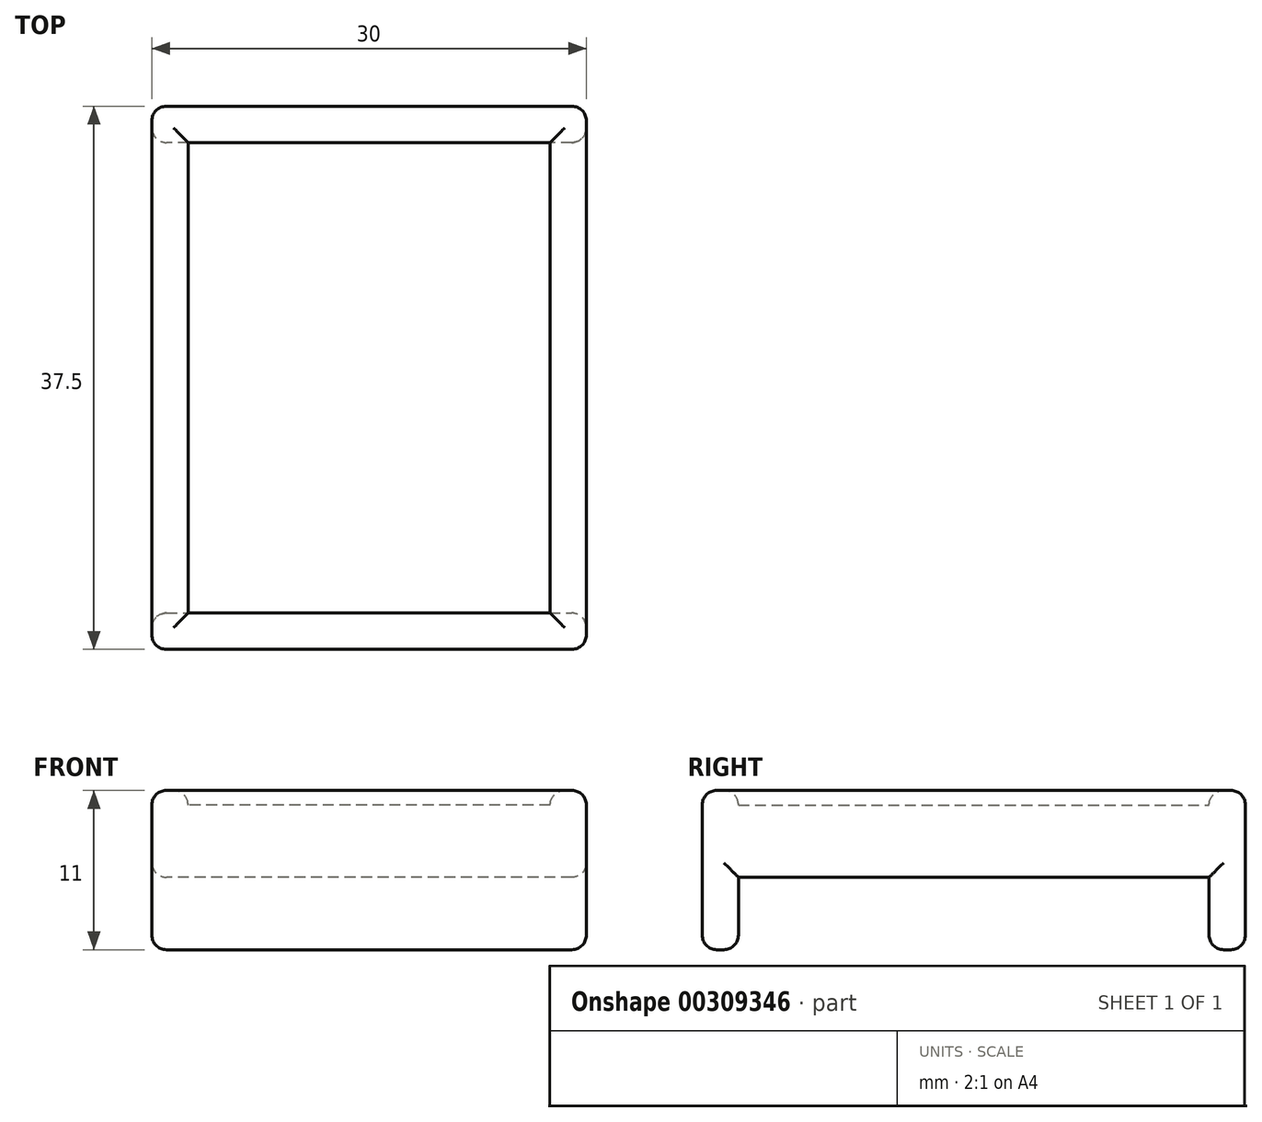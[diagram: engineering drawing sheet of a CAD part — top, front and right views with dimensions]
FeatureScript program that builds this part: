
annotation { "Feature Type Name" : "Feature", "Feature Type Description" : "" }
export const myFeature = defineFeature(function(context is Context, id is Id, definition is map)
    precondition{}
    {
        {
            var Q0;
            Q0=qCreatedBy(makeId("Top.planeOp"),FACE);
            var sketch = newSketch(context, id + "F0", { "sketchPlane" : qUnion([Q0])});
            skLineSegment(sketch, "E0.bottom", {"start": v(-12.5, 16.25) * mm, "end": v(12.5, 16.25) * mm});
            skLineSegment(sketch, "E0.top", {"start": v(-12.5, -16.25) * mm, "end": v(12.5, -16.25) * mm});
            skLineSegment(sketch, "E0.left", {"start": v(-12.5, 16.25) * mm, "end": v(-12.5, -16.25) * mm});
            skLineSegment(sketch, "E0.right", {"start": v(12.5, 16.25) * mm, "end": v(12.5, -16.25) * mm});
            skPoint(sketch, "E0.middle", {"position": v(0, 0) * mm});
            skLineSegment(sketch, "E1.bottom", {"start": v(-15, 18.75) * mm, "end": v(15, 18.75) * mm});
            skLineSegment(sketch, "E1.top", {"start": v(-15, -18.75) * mm, "end": v(15, -18.75) * mm});
            skLineSegment(sketch, "E1.left", {"start": v(-15, 18.75) * mm, "end": v(-15, -18.75) * mm});
            skLineSegment(sketch, "E1.right", {"start": v(15, 18.75) * mm, "end": v(15, -18.75) * mm});
            skLineSegment(sketch, "E2", {"start": v(-12.5, 16.25) * mm, "end": v(-15, 16.25) * mm});
            skLineSegment(sketch, "E3", {"start": v(12.5, 16.25) * mm, "end": v(15, 16.25) * mm});
            skLineSegment(sketch, "E4", {"start": v(-12.5, -16.25) * mm, "end": v(-15, -16.25) * mm});
            skLineSegment(sketch, "E5", {"start": v(12.5, -16.25) * mm, "end": v(15, -16.25) * mm});
            skSolve(sketch);
        }
        {
            var Q0;
            Q0=makeQuery(id+"F0.imprint","IMPRINT",FACE,{"disambiguationData":[TD([[makeQuery(id+"F0.imprint","IMPRINT",EDGE,{"derivedFrom":sQuery(id+"F0.wireOp",EDGE,"E0.bottom")}),-1.0]])]});
            var Q1;
            Q1=makeQuery(id+"F0.imprint","IMPRINT",FACE,{"disambiguationData":[TD([[makeQuery(id+"F0.imprint","IMPRINT",EDGE,{"derivedFrom":sQuery(id+"F0.wireOp",EDGE,"E0.bottom")}),1.0]])]});
            var Q2;
            Q2=makeQuery(id+"F0.imprint","IMPRINT",FACE,{"disambiguationData":[TD([[makeQuery(id+"F0.imprint","IMPRINT",EDGE,{"derivedFrom":sQuery(id+"F0.wireOp",EDGE,"E0.left")}),-1.0]])]});
            var Q3;
            Q3=makeQuery(id+"F0.imprint","IMPRINT",FACE,{"disambiguationData":[TD([[makeQuery(id+"F0.imprint","IMPRINT",EDGE,{"derivedFrom":sQuery(id+"F0.wireOp",EDGE,"E0.top")}),-1.0]])]});
            var Q4;
            Q4=makeQuery(id+"F0.imprint","IMPRINT",FACE,{"disambiguationData":[TD([[makeQuery(id+"F0.imprint","IMPRINT",EDGE,{"derivedFrom":sQuery(id+"F0.wireOp",EDGE,"E0.right")}),1.0]])]});
            extrude(context, id + "F1", {"entities" : qUnion([Q0, Q1, Q2, Q3, Q4]), "depth" : 5 * mm});
        }
        {
            var Q0;
            Q0=makeQuery(id+"F0.imprint","IMPRINT",FACE,{"disambiguationData":[TD([[makeQuery(id+"F0.imprint","IMPRINT",EDGE,{"derivedFrom":sQuery(id+"F0.wireOp",EDGE,"E0.bottom")}),1.0]])]});
            var Q1;
            Q1=makeQuery(id+"F0.imprint","IMPRINT",FACE,{"disambiguationData":[TD([[makeQuery(id+"F0.imprint","IMPRINT",EDGE,{"derivedFrom":sQuery(id+"F0.wireOp",EDGE,"E0.left")}),-1.0]])]});
            var Q2;
            Q2=makeQuery(id+"F0.imprint","IMPRINT",FACE,{"disambiguationData":[TD([[makeQuery(id+"F0.imprint","IMPRINT",EDGE,{"derivedFrom":sQuery(id+"F0.wireOp",EDGE,"E0.top")}),-1.0]])]});
            var Q3;
            Q3=makeQuery(id+"F0.imprint","IMPRINT",FACE,{"disambiguationData":[TD([[makeQuery(id+"F0.imprint","IMPRINT",EDGE,{"derivedFrom":sQuery(id+"F0.wireOp",EDGE,"E0.right")}),1.0]])]});
            extrude(context, id + "F2", {"entities" : qUnion([Q0, Q1, Q2, Q3]), "operationType" : NewBodyOperationType.ADD, "depth" : 6 * mm});
        }
        {
            var Q0;
            Q0=makeQuery(id+"F0.imprint","IMPRINT",FACE,{"disambiguationData":[TD([[makeQuery(id+"F0.imprint","IMPRINT",EDGE,{"derivedFrom":sQuery(id+"F0.wireOp",EDGE,"E0.top")}),-1.0]])]});
            var Q1;
            Q1=makeQuery(id+"F0.imprint","IMPRINT",FACE,{"disambiguationData":[TD([[makeQuery(id+"F0.imprint","IMPRINT",EDGE,{"derivedFrom":sQuery(id+"F0.wireOp",EDGE,"E0.bottom")}),1.0]])]});
            extrude(context, id + "F3", {"entities" : qUnion([Q0, Q1]), "operationType" : NewBodyOperationType.ADD, "oppositeDirection" : true, "depth" : 5 * mm});
        }
        {
            var Q0;
            Q0=makeQuery(id+"F3.opExtrude","CAP_FACE",FACE,{"disambiguationData":[OSD([sQuery(id+"F0.wireOp",EDGE,"E0.bottom"),sQuery(id+"F0.wireOp",EDGE,"E1.bottom"),sQuery(id+"F0.wireOp",EDGE,"E1.left"),sQuery(id+"F0.wireOp",EDGE,"E1.right"),sQuery(id+"F0.wireOp",EDGE,"E2"),sQuery(id+"F0.wireOp",EDGE,"E3")])],"isStart":false});
            var Q1;
            Q1=makeQuery(id+"F3.opExtrude","CAP_FACE",FACE,{"disambiguationData":[OSD([sQuery(id+"F0.wireOp",EDGE,"E0.top"),sQuery(id+"F0.wireOp",EDGE,"E1.top"),sQuery(id+"F0.wireOp",EDGE,"E1.left"),sQuery(id+"F0.wireOp",EDGE,"E1.right"),sQuery(id+"F0.wireOp",EDGE,"E4"),sQuery(id+"F0.wireOp",EDGE,"E5")])],"isStart":false});
            var Q2;
            Q2=makeQuery(id+"F2.opExtrude","CAP_FACE",FACE,{"disambiguationData":[OSD([sQuery(id+"F0.wireOp",EDGE,"E0.bottom"),sQuery(id+"F0.wireOp",EDGE,"E0.top"),sQuery(id+"F0.wireOp",EDGE,"E0.left"),sQuery(id+"F0.wireOp",EDGE,"E0.right"),sQuery(id+"F0.wireOp",EDGE,"E1.bottom"),sQuery(id+"F0.wireOp",EDGE,"E1.top"),sQuery(id+"F0.wireOp",EDGE,"E1.left"),sQuery(id+"F0.wireOp",EDGE,"E1.right")])],"isStart":false});
            var Q3;
            {var subQ0=sQuery(id+"F0.wireOp",EDGE,"E1.left");Q3=makeQuery(id+"F3.boolean.opBoolean","MERGE",FACE,{"derivedFrom":[makeQuery(id+"F2.boolean.opBoolean","MERGE",FACE,{"derivedFrom":[makeQuery(id+"F1.opExtrude","SWEPT_FACE",FACE,{"disambiguationData":[OSD([subQ0])]}),makeQuery(id+"F2.opExtrude","SWEPT_FACE",FACE,{"disambiguationData":[OSD([subQ0])]})]}),makeQuery(id+"F3.opExtrude","SWEPT_FACE",FACE,{"disambiguationData":[OSD([subQ0]),TDD([makeQuery(id+"F0.imprint","IMPRINT",EDGE,{"disambiguationData":[TD([[makeQuery(id+"F0.imprint","INTERSECT",VERTEX,{"derivedFrom":[sQuery(id+"F0.wireOp",EDGE,"E1.bottom"),subQ0]}),-1.0]])],"derivedFrom":subQ0})])]}),makeQuery(id+"F3.opExtrude","SWEPT_FACE",FACE,{"disambiguationData":[OSD([subQ0]),TDD([makeQuery(id+"F0.imprint","IMPRINT",EDGE,{"disambiguationData":[TD([[makeQuery(id+"F0.imprint","INTERSECT",VERTEX,{"derivedFrom":[sQuery(id+"F0.wireOp",EDGE,"E1.top"),subQ0]}),1.0]])],"derivedFrom":subQ0})])]})]});}
            var Q4;
            {var subQ0=sQuery(id+"F0.wireOp",EDGE,"E1.bottom");Q4=makeQuery(id+"F3.boolean.opBoolean","MERGE",FACE,{"derivedFrom":[makeQuery(id+"F2.boolean.opBoolean","MERGE",FACE,{"derivedFrom":[makeQuery(id+"F1.opExtrude","SWEPT_FACE",FACE,{"disambiguationData":[OSD([subQ0])]}),makeQuery(id+"F2.opExtrude","SWEPT_FACE",FACE,{"disambiguationData":[OSD([subQ0])]})]}),makeQuery(id+"F3.opExtrude","SWEPT_FACE",FACE,{"disambiguationData":[OSD([subQ0])]})]});}
            var Q5;
            {var subQ0=sQuery(id+"F0.wireOp",EDGE,"E1.right");Q5=makeQuery(id+"F3.boolean.opBoolean","MERGE",FACE,{"derivedFrom":[makeQuery(id+"F2.boolean.opBoolean","MERGE",FACE,{"derivedFrom":[makeQuery(id+"F1.opExtrude","SWEPT_FACE",FACE,{"disambiguationData":[OSD([subQ0])]}),makeQuery(id+"F2.opExtrude","SWEPT_FACE",FACE,{"disambiguationData":[OSD([subQ0])]})]}),makeQuery(id+"F3.opExtrude","SWEPT_FACE",FACE,{"disambiguationData":[OSD([subQ0]),TDD([makeQuery(id+"F0.imprint","IMPRINT",EDGE,{"disambiguationData":[TD([[makeQuery(id+"F0.imprint","INTERSECT",VERTEX,{"derivedFrom":[sQuery(id+"F0.wireOp",EDGE,"E1.bottom"),subQ0]}),-1.0]])],"derivedFrom":subQ0})])]}),makeQuery(id+"F3.opExtrude","SWEPT_FACE",FACE,{"disambiguationData":[OSD([subQ0]),TDD([makeQuery(id+"F0.imprint","IMPRINT",EDGE,{"disambiguationData":[TD([[makeQuery(id+"F0.imprint","INTERSECT",VERTEX,{"derivedFrom":[sQuery(id+"F0.wireOp",EDGE,"E1.top"),subQ0]}),1.0]])],"derivedFrom":subQ0})])]})]});}
            var Q6;
            {var subQ0=sQuery(id+"F0.wireOp",EDGE,"E1.top");Q6=makeQuery(id+"F3.boolean.opBoolean","MERGE",FACE,{"derivedFrom":[makeQuery(id+"F2.boolean.opBoolean","MERGE",FACE,{"derivedFrom":[makeQuery(id+"F1.opExtrude","SWEPT_FACE",FACE,{"disambiguationData":[OSD([subQ0])]}),makeQuery(id+"F2.opExtrude","SWEPT_FACE",FACE,{"disambiguationData":[OSD([subQ0])]})]}),makeQuery(id+"F3.opExtrude","SWEPT_FACE",FACE,{"disambiguationData":[OSD([subQ0])]})]});}
            fillet(context, id + "F4", {"entities" : qUnion([Q0, Q1, Q2, Q3, Q4, Q5, Q6]), "radius" : 1 * mm, "tangentPropagation" : true, "allowEdgeOverflow" : false});
        }
    });
